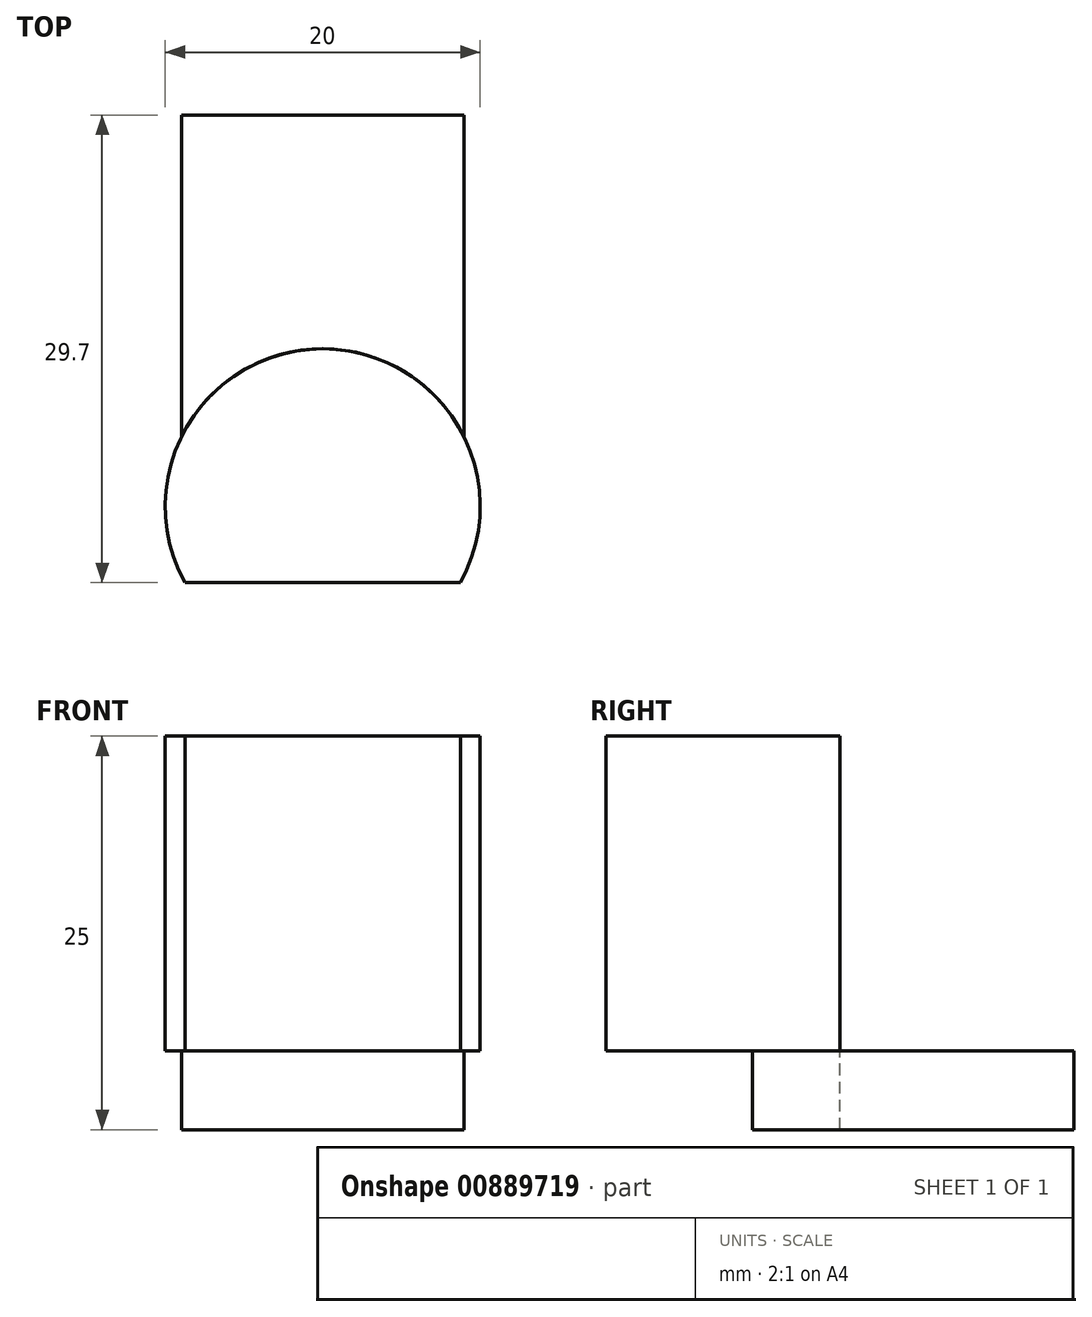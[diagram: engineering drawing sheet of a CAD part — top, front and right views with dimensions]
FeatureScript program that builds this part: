
annotation { "Feature Type Name" : "Feature", "Feature Type Description" : "" }
export const myFeature = defineFeature(function(context is Context, id is Id, definition is map)
    precondition{}
    {
        {
            var Q0;
            Q0=qCreatedBy(makeId("Top.planeOp"),FACE);
            var sketch = newSketch(context, id + "F0", { "sketchPlane" : qUnion([Q0])});
            skCircle(sketch, "E0", {"center": v(0, 0) * mm, "radius": 10 * mm});
            skPoint(sketch, "E1", {"position": v(0, 10) * mm});
            skLineSegment(sketch, "E2.bottom", {"start": v(8.96, 24.85) * mm, "end": v(-8.95, 24.85) * mm});
            skLineSegment(sketch, "E2.top", {"start": v(8.96, -4.85) * mm, "end": v(-8.95, -4.85) * mm});
            skLineSegment(sketch, "E2.left", {"start": v(8.96, 24.85) * mm, "end": v(8.96, -4.85) * mm});
            skLineSegment(sketch, "E2.right", {"start": v(-8.95, 24.85) * mm, "end": v(-8.95, -4.85) * mm});
            skSolve(sketch);
        }
        {
            var Q0;
            {var subQ1=sQuery(id+"F0.wireOp",EDGE,"E0");var subQ6=sQuery(id+"F0.wireOp",EDGE,"E2.right");var subQ8=makeQuery(id+"F0.imprint","INTERSECT",VERTEX,{"disambiguationData":[OD(0.0)],"derivedFrom":[subQ1,subQ6]});Q0=makeQuery(id+"F0.imprint","IMPRINT",FACE,{"disambiguationData":[TD([[makeQuery(id+"F0.imprint","IMPRINT",EDGE,{"disambiguationData":[TD([[subQ8,1.0]])],"derivedFrom":subQ1}),1.0]])]});}
            var Q1;
            {var subQ0=sQuery(id+"F0.wireOp",EDGE,"E2.left");var subQ1=sQuery(id+"F0.wireOp",EDGE,"E0");var subQ2=makeQuery(id+"F0.imprint","INTERSECT",VERTEX,{"disambiguationData":[OD(0.0)],"derivedFrom":[subQ1,subQ0]});Q1=makeQuery(id+"F0.imprint","IMPRINT",FACE,{"disambiguationData":[TD([[makeQuery(id+"F0.imprint","IMPRINT",EDGE,{"disambiguationData":[TD([[subQ2,1.0]])],"derivedFrom":subQ1}),1.0]])]});}
            var Q2;
            {var subQ0=sQuery(id+"F0.wireOp",EDGE,"E2.top");var subQ1=sQuery(id+"F0.wireOp",EDGE,"E0");var subQ2=makeQuery(id+"F0.imprint","INTERSECT",VERTEX,{"disambiguationData":[OD(0.0)],"derivedFrom":[subQ1,subQ0]});Q2=makeQuery(id+"F0.imprint","IMPRINT",FACE,{"disambiguationData":[TD([[makeQuery(id+"F0.imprint","IMPRINT",EDGE,{"disambiguationData":[TD([[subQ2,-1.0]])],"derivedFrom":subQ1}),1.0]])]});}
            var Q3;
            {var subQ0=sQuery(id+"F0.wireOp",EDGE,"E2.right");var subQ1=sQuery(id+"F0.wireOp",EDGE,"E0");var subQ2=makeQuery(id+"F0.imprint","INTERSECT",VERTEX,{"disambiguationData":[OD(0.0)],"derivedFrom":[subQ1,subQ0]});Q3=makeQuery(id+"F0.imprint","IMPRINT",FACE,{"disambiguationData":[TD([[makeQuery(id+"F0.imprint","IMPRINT",EDGE,{"disambiguationData":[TD([[subQ2,-1.0]])],"derivedFrom":subQ1}),1.0]])]});}
            var Q4;
            Q4=sQuery(id+"F0.wireOp",EDGE,"E0");
            extrude(context, id + "F1", {"entities" : qUnion([Q0, Q1, Q2, Q3]), "surfaceOperationType" : NewSurfaceOperationType.ADD, "surfaceEntities" : qUnion([Q4]), "depth" : 20 * mm, "offsetDistance" : 25 * mm});
        }
        {
            var Q0;
            Q0 = qSketchRegion(id + "F0", true);
            var sketch = newSketch(context, id + "F2", { "sketchPlane" : qUnion([Q0])});
            skSolve(sketch);
        }
        {
            var Q0;
            {var subQ5=sQuery(id+"F0.wireOp",EDGE,"E2.bottom");Q0=makeQuery(id+"F2.imprint","IMPRINT",FACE,{"disambiguationData":[TD([[makeQuery(id+"F2.imprint","IMPRINT",EDGE,{"derivedFrom":makeQuery(id+"F0.imprint","IMPRINT",EDGE,{"derivedFrom":subQ5})}),1.0]])]});}
            var Q1;
            {var subQ1=sQuery(id+"F0.wireOp",EDGE,"E0");var subQ6=sQuery(id+"F0.wireOp",EDGE,"E2.right");var subQ8=makeQuery(id+"F0.imprint","INTERSECT",VERTEX,{"disambiguationData":[OD(0.0)],"derivedFrom":[subQ1,subQ6]});Q1=makeQuery(id+"F2.imprint","IMPRINT",FACE,{"disambiguationData":[TD([[makeQuery(id+"F2.imprint","IMPRINT",EDGE,{"derivedFrom":makeQuery(id+"F0.imprint","IMPRINT",EDGE,{"disambiguationData":[TD([[subQ8,1.0]])],"derivedFrom":subQ1})}),1.0]])]});}
            var Q2;
            {var subQ0=sQuery(id+"F0.wireOp",EDGE,"E2.top");var subQ1=sQuery(id+"F0.wireOp",EDGE,"E0");var subQ2=makeQuery(id+"F0.imprint","INTERSECT",VERTEX,{"disambiguationData":[OD(0.0)],"derivedFrom":[subQ1,subQ0]});Q2=makeQuery(id+"F2.imprint","IMPRINT",FACE,{"disambiguationData":[TD([[makeQuery(id+"F2.imprint","IMPRINT",EDGE,{"derivedFrom":makeQuery(id+"F0.imprint","IMPRINT",EDGE,{"disambiguationData":[TD([[subQ2,-1.0]])],"derivedFrom":subQ1})}),1.0]])]});}
            var Q3;
            {var subQ0=sQuery(id+"F0.wireOp",EDGE,"E2.right");var subQ1=sQuery(id+"F0.wireOp",EDGE,"E0");var subQ2=makeQuery(id+"F0.imprint","INTERSECT",VERTEX,{"disambiguationData":[OD(0.0)],"derivedFrom":[subQ1,subQ0]});Q3=makeQuery(id+"F2.imprint","IMPRINT",FACE,{"disambiguationData":[TD([[makeQuery(id+"F2.imprint","IMPRINT",EDGE,{"derivedFrom":makeQuery(id+"F0.imprint","IMPRINT",EDGE,{"disambiguationData":[TD([[subQ2,-1.0]])],"derivedFrom":subQ1})}),1.0]])]});}
            var Q4;
            {var subQ0=sQuery(id+"F0.wireOp",EDGE,"E2.left");var subQ1=sQuery(id+"F0.wireOp",EDGE,"E0");var subQ2=makeQuery(id+"F0.imprint","INTERSECT",VERTEX,{"disambiguationData":[OD(0.0)],"derivedFrom":[subQ1,subQ0]});Q4=makeQuery(id+"F2.imprint","IMPRINT",FACE,{"disambiguationData":[TD([[makeQuery(id+"F2.imprint","IMPRINT",EDGE,{"derivedFrom":makeQuery(id+"F0.imprint","IMPRINT",EDGE,{"disambiguationData":[TD([[subQ2,1.0]])],"derivedFrom":subQ1})}),1.0]])]});}
            extrude(context, id + "F3", {"entities" : qUnion([Q0, Q1, Q2, Q3, Q4]), "operationType" : NewBodyOperationType.ADD, "oppositeDirection" : true, "depth" : 5 * mm, "offsetDistance" : 25 * mm});
        }
    });
